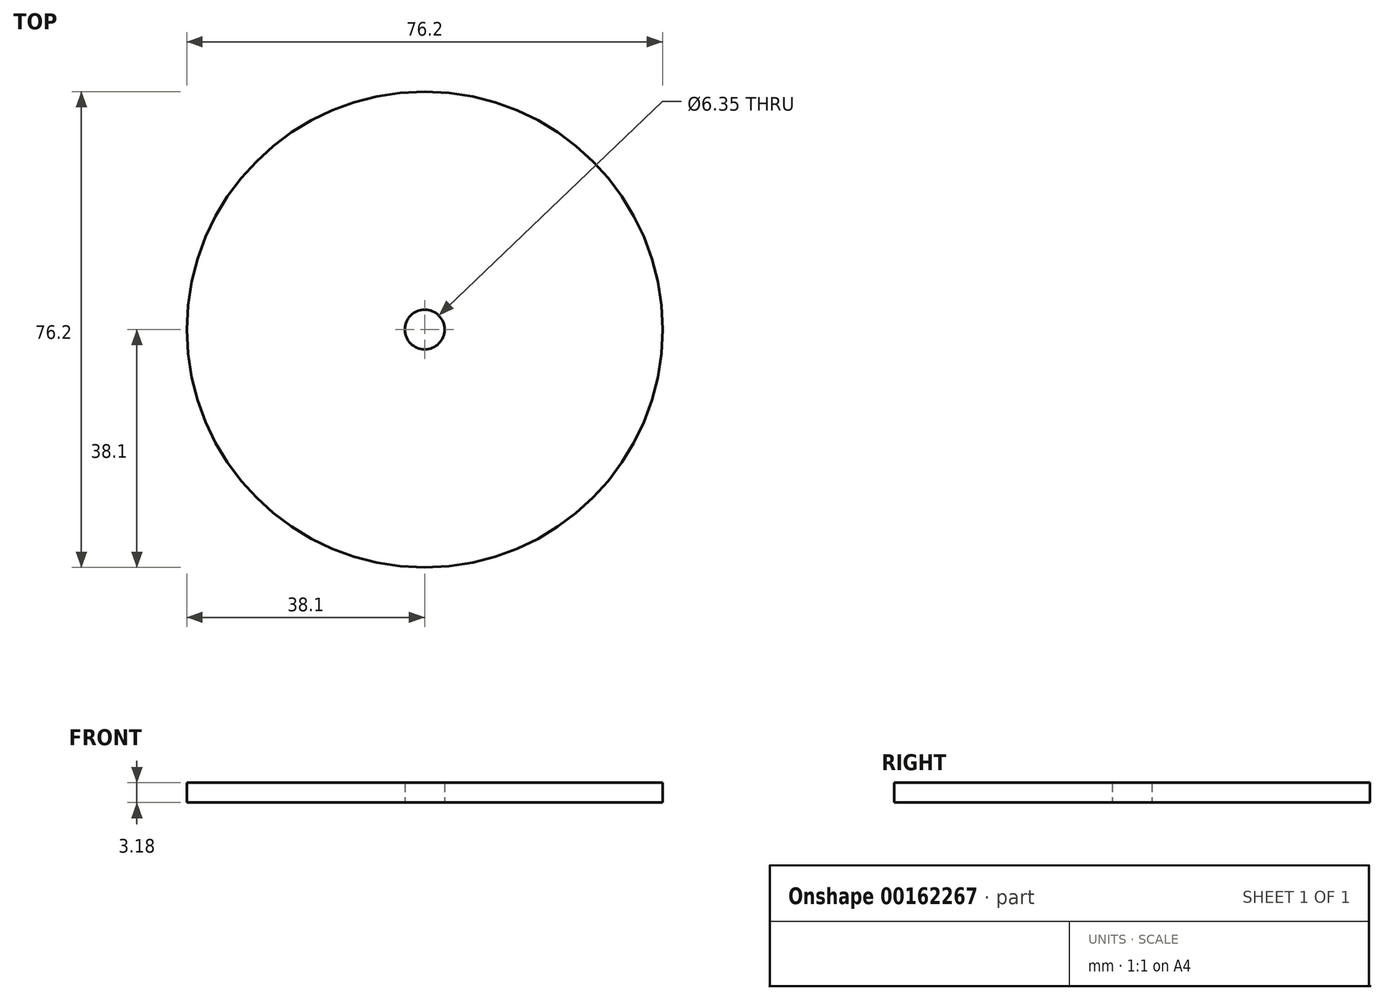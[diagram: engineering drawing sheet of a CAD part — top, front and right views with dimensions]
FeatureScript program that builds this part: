
annotation { "Feature Type Name" : "Feature", "Feature Type Description" : "" }
export const myFeature = defineFeature(function(context is Context, id is Id, definition is map)
    precondition{}
    {
        {
            var Q0;
            Q0=qCreatedBy(makeId("Top.planeOp"),FACE);
            var sketch = newSketch(context, id + "F0", { "sketchPlane" : qUnion([Q0])});
            skCircle(sketch, "E0", {"center": v(0, 0) * mm, "radius": 38.1 * mm});
            skCircle(sketch, "E1", {"center": v(0, 0) * mm, "radius": 3.18 * mm});
            skSolve(sketch);
        }
        {
            var Q0;
            Q0=makeQuery(id+"F0.imprint","IMPRINT",FACE,{"disambiguationData":[TD([[makeQuery(id+"F0.imprint","IMPRINT",EDGE,{"derivedFrom":sQuery(id+"F0.wireOp",EDGE,"E0")}),1.0]])]});
            extrude(context, id + "F1", {"entities" : qUnion([Q0]), "depth" : 3.17 * mm});
        }
    });
